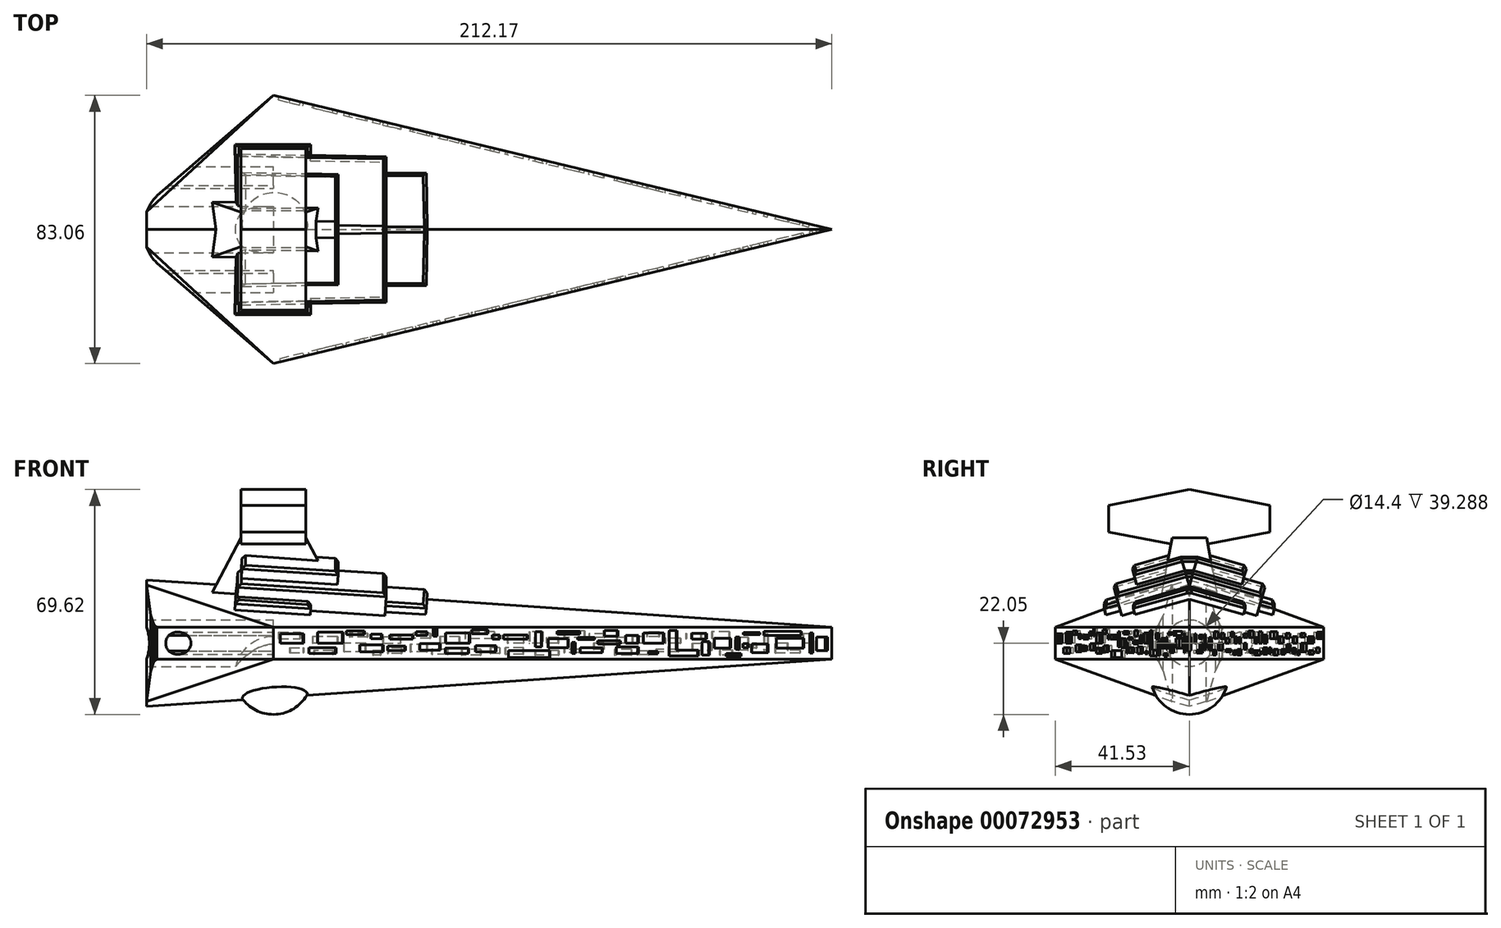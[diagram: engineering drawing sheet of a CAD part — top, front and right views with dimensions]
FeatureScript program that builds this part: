
annotation { "Feature Type Name" : "Feature", "Feature Type Description" : "" }
export const myFeature = defineFeature(function(context is Context, id is Id, definition is map)
    precondition{}
    {
        {
            var Q0;
            Q0=qCreatedBy(makeId("Top.planeOp"),FACE);
            var sketch = newSketch(context, id + "F0", { "sketchPlane" : qUnion([Q0])});
            skLineSegment(sketch, "E0", {"start": v(0, -41.53) * mm, "end": v(-48.04, 0) * mm});
            skLineSegment(sketch, "E1", {"start": v(-48.04, 0) * mm, "end": v(0, 41.53) * mm});
            skLineSegment(sketch, "E2", {"start": v(0, 41.53) * mm, "end": v(172.88, 0) * mm});
            skLineSegment(sketch, "E3", {"start": v(172.88, 0) * mm, "end": v(0, -41.53) * mm});
            skSolve(sketch);
        }
        {
            var Q0;
            Q0=makeQuery(id+"F0.imprint","IMPRINT",FACE,{"disambiguationData":[TD([[makeQuery(id+"F0.imprint","IMPRINT",EDGE,{"derivedFrom":sQuery(id+"F0.wireOp",EDGE,"E0")}),-1.0]])]});
            extrude(context, id + "F1", {"entities" : qUnion([Q0]), "depth" : 5 * mm});
        }
        {
            var Q0;
            Q0=qCreatedBy(makeId("Top.planeOp"),FACE);
            cPlane(context, id + "F2", {"entities" : qUnion([Q0]), "cplaneType" : CPlaneType.OFFSET, "offset" : 20 * mm, "width" : 150 * mm, "height" : 150 * mm});
        }
        {
            var Q0;
            Q0=qCreatedBy(id+"F2.planeOp",FACE);
            var sketch = newSketch(context, id + "F3", { "sketchPlane" : qUnion([Q0])});
            skPoint(sketch, "E4", {"position": v(-45.15, 0) * mm});
            skSolve(sketch);
        }
        {
            var Q1;
            Q1=sQuery(id+"F3.wireOp",VERTEX,"E4");
            var Q2;
            Q2=makeQuery(id+"F1.opExtrude","CAP_FACE",FACE,{"disambiguationData":[OSD([sQuery(id+"F0.wireOp",EDGE,"E0"),sQuery(id+"F0.wireOp",EDGE,"E1"),sQuery(id+"F0.wireOp",EDGE,"E2"),sQuery(id+"F0.wireOp",EDGE,"E3")])],"isStart":false});
            loft(context, id + "F4", {"operationType" : NewBodyOperationType.ADD, "sheetProfilesArray" : [{ "sheetProfileEntities" : qUnion([Q1]) }, { "sheetProfileEntities" : qUnion([Q2]) }]});
        }
        {
            var Q0;
            Q0=makeQuery(id+"F1.opExtrude","SWEPT_BODY",BODY,{"disambiguationData":[OSD([sQuery(id+"F0.wireOp",EDGE,"E0"),sQuery(id+"F0.wireOp",EDGE,"E1"),sQuery(id+"F0.wireOp",EDGE,"E2"),sQuery(id+"F0.wireOp",EDGE,"E3")])]});
            var Q1;
            Q1=qCreatedBy(makeId("Top.planeOp"),FACE);
            mirror(context, id + "F5", {"operationType" : NewBodyOperationType.ADD, "entities" : qUnion([Q0]), "mirrorPlane" : qUnion([Q1])});
        }
        {
            var Q0;
            {var subQ0=makeQuery(id+"F1.opExtrude","SWEPT_EDGE",EDGE,{"disambiguationData":[OSD([sQuery(id+"F0.wireOp",EDGE,"E0"),sQuery(id+"F0.wireOp",EDGE,"E1")])]});Q0=makeQuery(id+"F5.boolean.opBoolean","MERGE",EDGE,{"derivedFrom":[subQ0,makeQuery(id+"F5.opPattern","COPY",EDGE,{"derivedFrom":subQ0,"instanceName":"1"})]});}
            chamfer(context, id + "F6", {"entities" : qUnion([Q0]), "width" : 10 * mm, "tangentPropagation" : true});
        }
        {
            var Q0;
            {var subQ0=sQuery(id+"F0.wireOp",EDGE,"E0");var subQ1=makeQuery(id+"F1.opExtrude","SWEPT_FACE",FACE,{"disambiguationData":[OSD([subQ0])]});var subQ2=makeQuery(id+"F1.opExtrude","SWEPT_EDGE",EDGE,{"disambiguationData":[OSD([subQ0,sQuery(id+"F0.wireOp",EDGE,"E1")])]});Q0=makeQuery(id+"F6.opChamfer","BLEND_EDGE",EDGE,{"blendedFrom":[makeQuery(id+"F5.boolean.opBoolean","MERGE",EDGE,{"derivedFrom":[subQ2,makeQuery(id+"F5.opPattern","COPY",EDGE,{"derivedFrom":subQ2,"instanceName":"1"})]}),makeQuery(id+"F5.boolean.opBoolean","MERGE",FACE,{"derivedFrom":[subQ1,makeQuery(id+"F5.opPattern","COPY",FACE,{"derivedFrom":subQ1,"instanceName":"1"})]})],"blendedInto":[makeQuery(id+"F5.boolean.opBoolean","MERGE",FACE,{"derivedFrom":[subQ1,makeQuery(id+"F5.opPattern","COPY",FACE,{"derivedFrom":subQ1,"instanceName":"1"})]})]});}
            chamfer(context, id + "F7", {"entities" : qUnion([Q0]), "width" : 5 * mm, "tangentPropagation" : true});
        }
        {
            var Q0;
            {var subQ0=sQuery(id+"F0.wireOp",EDGE,"E1");var subQ1=makeQuery(id+"F1.opExtrude","SWEPT_FACE",FACE,{"disambiguationData":[OSD([subQ0])]});var subQ2=makeQuery(id+"F1.opExtrude","SWEPT_EDGE",EDGE,{"disambiguationData":[OSD([sQuery(id+"F0.wireOp",EDGE,"E0"),subQ0])]});Q0=makeQuery(id+"F6.opChamfer","BLEND_EDGE",EDGE,{"blendedFrom":[makeQuery(id+"F5.boolean.opBoolean","MERGE",EDGE,{"derivedFrom":[subQ2,makeQuery(id+"F5.opPattern","COPY",EDGE,{"derivedFrom":subQ2,"instanceName":"1"})]}),makeQuery(id+"F5.boolean.opBoolean","MERGE",FACE,{"derivedFrom":[subQ1,makeQuery(id+"F5.opPattern","COPY",FACE,{"derivedFrom":subQ1,"instanceName":"1"})]})],"blendedInto":[makeQuery(id+"F5.boolean.opBoolean","MERGE",FACE,{"derivedFrom":[subQ1,makeQuery(id+"F5.opPattern","COPY",FACE,{"derivedFrom":subQ1,"instanceName":"1"})]})]});}
            chamfer(context, id + "F8", {"entities" : qUnion([Q0]), "width" : 5 * mm, "tangentPropagation" : true});
        }
        {
            var Q0;
            {var subQ0=sQuery(id+"F0.wireOp",EDGE,"E1");var subQ1=makeQuery(id+"F1.opExtrude","SWEPT_FACE",FACE,{"disambiguationData":[OSD([subQ0])]});var subQ2=makeQuery(id+"F5.boolean.opBoolean","MERGE",FACE,{"derivedFrom":[subQ1,makeQuery(id+"F5.opPattern","COPY",FACE,{"derivedFrom":subQ1,"instanceName":"1"})]});var subQ3=makeQuery(id+"F1.opExtrude","SWEPT_EDGE",EDGE,{"disambiguationData":[OSD([sQuery(id+"F0.wireOp",EDGE,"E0"),subQ0])]});Q0=makeQuery(id+"F8.opChamfer","BLEND_EDGE",EDGE,{"blendedFrom":[makeQuery(id+"F6.opChamfer","BLEND_EDGE",EDGE,{"blendedFrom":[makeQuery(id+"F5.boolean.opBoolean","MERGE",EDGE,{"derivedFrom":[subQ3,makeQuery(id+"F5.opPattern","COPY",EDGE,{"derivedFrom":subQ3,"instanceName":"1"})]}),subQ2],"blendedInto":[subQ2]}),subQ2],"blendedInto":[subQ2]});}
            var Q1;
            {var subQ0=sQuery(id+"F0.wireOp",EDGE,"E0");var subQ1=makeQuery(id+"F1.opExtrude","SWEPT_FACE",FACE,{"disambiguationData":[OSD([subQ0])]});var subQ2=makeQuery(id+"F5.boolean.opBoolean","MERGE",FACE,{"derivedFrom":[subQ1,makeQuery(id+"F5.opPattern","COPY",FACE,{"derivedFrom":subQ1,"instanceName":"1"})]});var subQ3=makeQuery(id+"F1.opExtrude","SWEPT_EDGE",EDGE,{"disambiguationData":[OSD([subQ0,sQuery(id+"F0.wireOp",EDGE,"E1")])]});Q1=makeQuery(id+"F7.opChamfer","BLEND_EDGE",EDGE,{"blendedFrom":[makeQuery(id+"F6.opChamfer","BLEND_EDGE",EDGE,{"blendedFrom":[makeQuery(id+"F5.boolean.opBoolean","MERGE",EDGE,{"derivedFrom":[subQ3,makeQuery(id+"F5.opPattern","COPY",EDGE,{"derivedFrom":subQ3,"instanceName":"1"})]}),subQ2],"blendedInto":[subQ2]}),subQ2],"blendedInto":[subQ2]});}
            chamfer(context, id + "F9", {"entities" : qUnion([Q0, Q1]), "width" : 5 * mm, "tangentPropagation" : true});
        }
        {
            var Q0;
            {var subQ0=sQuery(id+"F0.wireOp",EDGE,"E1");var subQ1=makeQuery(id+"F1.opExtrude","SWEPT_FACE",FACE,{"disambiguationData":[OSD([subQ0])]});var subQ2=makeQuery(id+"F5.boolean.opBoolean","MERGE",FACE,{"derivedFrom":[subQ1,makeQuery(id+"F5.opPattern","COPY",FACE,{"derivedFrom":subQ1,"instanceName":"1"})]});var subQ3=subQ2;var subQ4=makeQuery(id+"F1.opExtrude","SWEPT_EDGE",EDGE,{"disambiguationData":[OSD([sQuery(id+"F0.wireOp",EDGE,"E0"),subQ0])]});Q0=makeQuery(id+"F9.opChamfer","BLEND_EDGE",EDGE,{"blendedFrom":[makeQuery(id+"F8.opChamfer","BLEND_EDGE",EDGE,{"blendedFrom":[makeQuery(id+"F6.opChamfer","BLEND_EDGE",EDGE,{"blendedFrom":[makeQuery(id+"F5.boolean.opBoolean","MERGE",EDGE,{"derivedFrom":[subQ4,makeQuery(id+"F5.opPattern","COPY",EDGE,{"derivedFrom":subQ4,"instanceName":"1"})]}),subQ2],"blendedInto":[subQ2]}),subQ3],"blendedInto":[subQ3]}),subQ3],"blendedInto":[subQ3]});}
            var Q1;
            {var subQ0=sQuery(id+"F0.wireOp",EDGE,"E0");var subQ1=makeQuery(id+"F1.opExtrude","SWEPT_FACE",FACE,{"disambiguationData":[OSD([subQ0])]});var subQ2=makeQuery(id+"F5.boolean.opBoolean","MERGE",FACE,{"derivedFrom":[subQ1,makeQuery(id+"F5.opPattern","COPY",FACE,{"derivedFrom":subQ1,"instanceName":"1"})]});var subQ3=subQ2;var subQ4=makeQuery(id+"F1.opExtrude","SWEPT_EDGE",EDGE,{"disambiguationData":[OSD([subQ0,sQuery(id+"F0.wireOp",EDGE,"E1")])]});Q1=makeQuery(id+"F9.opChamfer","BLEND_EDGE",EDGE,{"blendedFrom":[makeQuery(id+"F7.opChamfer","BLEND_EDGE",EDGE,{"blendedFrom":[makeQuery(id+"F6.opChamfer","BLEND_EDGE",EDGE,{"blendedFrom":[makeQuery(id+"F5.boolean.opBoolean","MERGE",EDGE,{"derivedFrom":[subQ4,makeQuery(id+"F5.opPattern","COPY",EDGE,{"derivedFrom":subQ4,"instanceName":"1"})]}),subQ2],"blendedInto":[subQ2]}),subQ3],"blendedInto":[subQ3]}),subQ3],"blendedInto":[subQ3]});}
            chamfer(context, id + "F10", {"entities" : qUnion([Q0, Q1]), "width" : 5 * mm, "tangentPropagation" : true});
        }
        {
            var Q0;
            {var subQ0=sQuery(id+"F0.wireOp",EDGE,"E1");var subQ1=makeQuery(id+"F1.opExtrude","SWEPT_FACE",FACE,{"disambiguationData":[OSD([subQ0])]});var subQ2=makeQuery(id+"F5.boolean.opBoolean","MERGE",FACE,{"derivedFrom":[subQ1,makeQuery(id+"F5.opPattern","COPY",FACE,{"derivedFrom":subQ1,"instanceName":"1"})]});var subQ3=subQ2;var subQ4=subQ3;var subQ5=makeQuery(id+"F1.opExtrude","SWEPT_EDGE",EDGE,{"disambiguationData":[OSD([sQuery(id+"F0.wireOp",EDGE,"E0"),subQ0])]});Q0=makeQuery(id+"F10.opChamfer","BLEND_EDGE",EDGE,{"blendedFrom":[makeQuery(id+"F9.opChamfer","BLEND_EDGE",EDGE,{"blendedFrom":[makeQuery(id+"F8.opChamfer","BLEND_EDGE",EDGE,{"blendedFrom":[makeQuery(id+"F6.opChamfer","BLEND_EDGE",EDGE,{"blendedFrom":[makeQuery(id+"F5.boolean.opBoolean","MERGE",EDGE,{"derivedFrom":[subQ5,makeQuery(id+"F5.opPattern","COPY",EDGE,{"derivedFrom":subQ5,"instanceName":"1"})]}),subQ2],"blendedInto":[subQ2]}),subQ3],"blendedInto":[subQ3]}),subQ4],"blendedInto":[subQ4]}),subQ4],"blendedInto":[subQ4]});}
            var Q1;
            {var subQ0=sQuery(id+"F0.wireOp",EDGE,"E0");var subQ1=makeQuery(id+"F1.opExtrude","SWEPT_FACE",FACE,{"disambiguationData":[OSD([subQ0])]});var subQ2=makeQuery(id+"F5.boolean.opBoolean","MERGE",FACE,{"derivedFrom":[subQ1,makeQuery(id+"F5.opPattern","COPY",FACE,{"derivedFrom":subQ1,"instanceName":"1"})]});var subQ3=subQ2;var subQ4=subQ3;var subQ5=makeQuery(id+"F1.opExtrude","SWEPT_EDGE",EDGE,{"disambiguationData":[OSD([subQ0,sQuery(id+"F0.wireOp",EDGE,"E1")])]});Q1=makeQuery(id+"F10.opChamfer","BLEND_EDGE",EDGE,{"blendedFrom":[makeQuery(id+"F9.opChamfer","BLEND_EDGE",EDGE,{"blendedFrom":[makeQuery(id+"F7.opChamfer","BLEND_EDGE",EDGE,{"blendedFrom":[makeQuery(id+"F6.opChamfer","BLEND_EDGE",EDGE,{"blendedFrom":[makeQuery(id+"F5.boolean.opBoolean","MERGE",EDGE,{"derivedFrom":[subQ5,makeQuery(id+"F5.opPattern","COPY",EDGE,{"derivedFrom":subQ5,"instanceName":"1"})]}),subQ2],"blendedInto":[subQ2]}),subQ3],"blendedInto":[subQ3]}),subQ4],"blendedInto":[subQ4]}),subQ4],"blendedInto":[subQ4]});}
            chamfer(context, id + "F11", {"entities" : qUnion([Q0, Q1]), "width" : 5 * mm, "tangentPropagation" : true});
        }
        {
            var Q0;
            {var subQ0=sQuery(id+"F0.wireOp",EDGE,"E1");var subQ1=makeQuery(id+"F1.opExtrude","SWEPT_FACE",FACE,{"disambiguationData":[OSD([subQ0])]});var subQ2=makeQuery(id+"F5.boolean.opBoolean","MERGE",FACE,{"derivedFrom":[subQ1,makeQuery(id+"F5.opPattern","COPY",FACE,{"derivedFrom":subQ1,"instanceName":"1"})]});var subQ3=subQ2;var subQ4=subQ3;var subQ5=subQ4;var subQ6=makeQuery(id+"F1.opExtrude","SWEPT_EDGE",EDGE,{"disambiguationData":[OSD([sQuery(id+"F0.wireOp",EDGE,"E0"),subQ0])]});Q0=makeQuery(id+"F11.opChamfer","BLEND_EDGE",EDGE,{"blendedFrom":[makeQuery(id+"F10.opChamfer","BLEND_EDGE",EDGE,{"blendedFrom":[makeQuery(id+"F9.opChamfer","BLEND_EDGE",EDGE,{"blendedFrom":[makeQuery(id+"F8.opChamfer","BLEND_EDGE",EDGE,{"blendedFrom":[makeQuery(id+"F6.opChamfer","BLEND_EDGE",EDGE,{"blendedFrom":[makeQuery(id+"F5.boolean.opBoolean","MERGE",EDGE,{"derivedFrom":[subQ6,makeQuery(id+"F5.opPattern","COPY",EDGE,{"derivedFrom":subQ6,"instanceName":"1"})]}),subQ2],"blendedInto":[subQ2]}),subQ3],"blendedInto":[subQ3]}),subQ4],"blendedInto":[subQ4]}),subQ5],"blendedInto":[subQ5]}),subQ5],"blendedInto":[subQ5]});}
            var Q1;
            {var subQ0=sQuery(id+"F0.wireOp",EDGE,"E0");var subQ1=makeQuery(id+"F1.opExtrude","SWEPT_FACE",FACE,{"disambiguationData":[OSD([subQ0])]});var subQ2=makeQuery(id+"F5.boolean.opBoolean","MERGE",FACE,{"derivedFrom":[subQ1,makeQuery(id+"F5.opPattern","COPY",FACE,{"derivedFrom":subQ1,"instanceName":"1"})]});var subQ3=subQ2;var subQ4=subQ3;var subQ5=subQ4;var subQ6=makeQuery(id+"F1.opExtrude","SWEPT_EDGE",EDGE,{"disambiguationData":[OSD([subQ0,sQuery(id+"F0.wireOp",EDGE,"E1")])]});Q1=makeQuery(id+"F11.opChamfer","BLEND_EDGE",EDGE,{"blendedFrom":[makeQuery(id+"F10.opChamfer","BLEND_EDGE",EDGE,{"blendedFrom":[makeQuery(id+"F9.opChamfer","BLEND_EDGE",EDGE,{"blendedFrom":[makeQuery(id+"F7.opChamfer","BLEND_EDGE",EDGE,{"blendedFrom":[makeQuery(id+"F6.opChamfer","BLEND_EDGE",EDGE,{"blendedFrom":[makeQuery(id+"F5.boolean.opBoolean","MERGE",EDGE,{"derivedFrom":[subQ6,makeQuery(id+"F5.opPattern","COPY",EDGE,{"derivedFrom":subQ6,"instanceName":"1"})]}),subQ2],"blendedInto":[subQ2]}),subQ3],"blendedInto":[subQ3]}),subQ4],"blendedInto":[subQ4]}),subQ5],"blendedInto":[subQ5]}),subQ5],"blendedInto":[subQ5]});}
            chamfer(context, id + "F12", {"entities" : qUnion([Q0, Q1]), "width" : 5 * mm, "tangentPropagation" : true});
        }
        {
            var Q0;
            Q0=qCreatedBy(makeId("Right.planeOp"),FACE);
            var sketch = newSketch(context, id + "F13", { "sketchPlane" : qUnion([Q0])});
            skCircle(sketch, "E5", {"center": v(0, 0) * mm, "radius": 7.2 * mm});
            skCircle(sketch, "E6", {"center": v(16.02, 0) * mm, "radius": 3.47 * mm});
            skCircle(sketch, "E7", {"center": v(-16.62, 0) * mm, "radius": 3.92 * mm});
            skSolve(sketch);
        }
        {
            var Q0;
            Q0 = qSketchRegion(id + "F13", true);
            extrude(context, id + "F14", {"entities" : qUnion([Q0]), "operationType" : NewBodyOperationType.REMOVE, "oppositeDirection" : true, "depth" : 99.65 * mm});
        }
        {
            var Q0;
            {var subQ0=makeQuery(id+"F1.opExtrude","SWEPT_FACE",FACE,{"disambiguationData":[OSD([sQuery(id+"F0.wireOp",EDGE,"E3")])]});Q0=makeQuery(id+"F5.boolean.opBoolean","MERGE",FACE,{"derivedFrom":[subQ0,makeQuery(id+"F5.opPattern","COPY",FACE,{"derivedFrom":subQ0,"instanceName":"1"})]});}
            var sketch = newSketch(context, id + "F15", { "sketchPlane" : qUnion([Q0])});
            skLineSegment(sketch, "E8.rect.bottom", {"start": v(0, 0) * mm, "end": v(-7.53, 0) * mm});
            skLineSegment(sketch, "E8.rect.top", {"start": v(0, 2.86) * mm, "end": v(-7.53, 2.86) * mm});
            skLineSegment(sketch, "E8.rect.left", {"start": v(0, 0) * mm, "end": v(0, 2.86) * mm});
            skLineSegment(sketch, "E8.rect.right", {"start": v(-7.53, 0) * mm, "end": v(-7.53, 2.86) * mm});
            skPoint(sketch, "E8.rect.middle", {"position": v(-3.77, 1.43) * mm});
            skLineSegment(sketch, "E9.rect.bottom", {"start": v(10.31, -3.23) * mm, "end": v(1.65, -3.23) * mm});
            skLineSegment(sketch, "E9.rect.top", {"start": v(10.31, -1.43) * mm, "end": v(1.65, -1.43) * mm});
            skLineSegment(sketch, "E9.rect.left", {"start": v(10.31, -3.23) * mm, "end": v(10.31, -1.43) * mm});
            skLineSegment(sketch, "E9.rect.right", {"start": v(1.65, -3.23) * mm, "end": v(1.65, -1.43) * mm});
            skPoint(sketch, "E9.rect.middle", {"position": v(5.98, -2.33) * mm});
            skLineSegment(sketch, "E10.rect.bottom", {"start": v(12.48, 0) * mm, "end": v(4.43, 0) * mm});
            skLineSegment(sketch, "E10.rect.top", {"start": v(12.48, 3.46) * mm, "end": v(4.43, 3.46) * mm});
            skLineSegment(sketch, "E10.rect.left", {"start": v(12.48, 0) * mm, "end": v(12.48, 3.46) * mm});
            skLineSegment(sketch, "E10.rect.right", {"start": v(4.43, 0) * mm, "end": v(4.43, 3.46) * mm});
            skPoint(sketch, "E10.rect.middle", {"position": v(8.46, 1.73) * mm});
            skLineSegment(sketch, "E11.rect.bottom", {"start": v(25.32, -2.63) * mm, "end": v(17.9, -2.63) * mm});
            skLineSegment(sketch, "E11.rect.top", {"start": v(25.32, -0.53) * mm, "end": v(17.9, -0.53) * mm});
            skLineSegment(sketch, "E11.rect.left", {"start": v(25.32, -2.63) * mm, "end": v(25.32, -0.53) * mm});
            skLineSegment(sketch, "E11.rect.right", {"start": v(17.9, -2.63) * mm, "end": v(17.9, -0.53) * mm});
            skPoint(sketch, "E11.rect.middle", {"position": v(21.6, -1.58) * mm});
            skLineSegment(sketch, "E12.rect.bottom", {"start": v(34.76, 1.28) * mm, "end": v(27.33, 1.28) * mm});
            skLineSegment(sketch, "E12.rect.top", {"start": v(34.76, 2.48) * mm, "end": v(27.33, 2.48) * mm});
            skLineSegment(sketch, "E12.rect.left", {"start": v(34.76, 1.28) * mm, "end": v(34.76, 2.48) * mm});
            skLineSegment(sketch, "E12.rect.right", {"start": v(27.33, 1.28) * mm, "end": v(27.33, 2.48) * mm});
            skPoint(sketch, "E12.rect.middle", {"position": v(31.04, 1.88) * mm});
            skLineSegment(sketch, "E13.rect.bottom", {"start": v(43.42, -2.18) * mm, "end": v(36.92, -2.18) * mm});
            skLineSegment(sketch, "E13.rect.top", {"start": v(43.42, -0.08) * mm, "end": v(36.92, -0.08) * mm});
            skLineSegment(sketch, "E13.rect.left", {"start": v(43.42, -2.18) * mm, "end": v(43.42, -0.08) * mm});
            skLineSegment(sketch, "E13.rect.right", {"start": v(36.92, -2.18) * mm, "end": v(36.92, -0.08) * mm});
            skPoint(sketch, "E13.rect.middle", {"position": v(40.17, -1.13) * mm});
            skLineSegment(sketch, "E14.rect.bottom", {"start": v(52.86, 0) * mm, "end": v(45.12, 0) * mm});
            skLineSegment(sketch, "E14.rect.top", {"start": v(52.86, 3.16) * mm, "end": v(45.12, 3.16) * mm});
            skLineSegment(sketch, "E14.rect.left", {"start": v(52.86, 0) * mm, "end": v(52.86, 3.16) * mm});
            skLineSegment(sketch, "E14.rect.right", {"start": v(45.12, 0) * mm, "end": v(45.12, 3.16) * mm});
            skPoint(sketch, "E14.rect.middle", {"position": v(48.99, 1.58) * mm});
            skLineSegment(sketch, "E15.rect.bottom", {"start": v(61.21, -2.63) * mm, "end": v(54.71, -2.63) * mm});
            skLineSegment(sketch, "E15.rect.top", {"start": v(61.21, -0.83) * mm, "end": v(54.71, -0.83) * mm});
            skLineSegment(sketch, "E15.rect.left", {"start": v(61.21, -2.63) * mm, "end": v(61.21, -0.83) * mm});
            skLineSegment(sketch, "E15.rect.right", {"start": v(54.71, -2.63) * mm, "end": v(54.71, -0.83) * mm});
            skPoint(sketch, "E15.rect.middle", {"position": v(57.96, -1.73) * mm});
            skLineSegment(sketch, "E16.rect.bottom", {"start": v(71.27, 1.28) * mm, "end": v(63.53, 1.28) * mm});
            skLineSegment(sketch, "E16.rect.top", {"start": v(71.27, 2.48) * mm, "end": v(63.53, 2.48) * mm});
            skLineSegment(sketch, "E16.rect.left", {"start": v(71.27, 1.28) * mm, "end": v(71.27, 2.48) * mm});
            skLineSegment(sketch, "E16.rect.right", {"start": v(63.53, 1.28) * mm, "end": v(63.53, 2.48) * mm});
            skPoint(sketch, "E16.rect.middle", {"position": v(67.4, 1.88) * mm});
            skLineSegment(sketch, "E17.rect.bottom", {"start": v(78.38, -2.33) * mm, "end": v(65.08, -2.33) * mm});
            skLineSegment(sketch, "E17.rect.top", {"start": v(78.38, -4.44) * mm, "end": v(65.08, -4.44) * mm});
            skLineSegment(sketch, "E17.rect.left", {"start": v(78.38, -2.33) * mm, "end": v(78.38, -4.44) * mm});
            skLineSegment(sketch, "E17.rect.right", {"start": v(65.08, -2.33) * mm, "end": v(65.08, -4.44) * mm});
            skPoint(sketch, "E17.rect.middle", {"position": v(71.73, -3.38) * mm});
            skLineSegment(sketch, "E18.rect.bottom", {"start": v(84.26, -1.43) * mm, "end": v(77.76, -1.43) * mm});
            skLineSegment(sketch, "E18.rect.top", {"start": v(84.26, 1.43) * mm, "end": v(77.76, 1.43) * mm});
            skLineSegment(sketch, "E18.rect.left", {"start": v(84.26, -1.43) * mm, "end": v(84.26, 1.43) * mm});
            skLineSegment(sketch, "E18.rect.right", {"start": v(77.76, -1.43) * mm, "end": v(77.76, 1.43) * mm});
            skPoint(sketch, "E18.rect.middle", {"position": v(81.01, 0) * mm});
            skLineSegment(sketch, "E19.rect.bottom", {"start": v(95.1, -1.43) * mm, "end": v(87.98, -1.43) * mm});
            skLineSegment(sketch, "E19.rect.top", {"start": v(95.1, -2.93) * mm, "end": v(87.98, -2.93) * mm});
            skLineSegment(sketch, "E19.rect.left", {"start": v(95.1, -1.43) * mm, "end": v(95.1, -2.93) * mm});
            skLineSegment(sketch, "E19.rect.right", {"start": v(87.98, -1.43) * mm, "end": v(87.98, -2.93) * mm});
            skPoint(sketch, "E19.rect.middle", {"position": v(91.53, -2.18) * mm});
            skLineSegment(sketch, "E20.rect.bottom", {"start": v(100.04, 2.18) * mm, "end": v(95.71, 2.18) * mm});
            skLineSegment(sketch, "E20.rect.top", {"start": v(100.04, 3.99) * mm, "end": v(95.71, 3.99) * mm});
            skLineSegment(sketch, "E20.rect.left", {"start": v(100.04, 2.18) * mm, "end": v(100.04, 3.99) * mm});
            skLineSegment(sketch, "E20.rect.right", {"start": v(95.71, 2.18) * mm, "end": v(95.71, 3.99) * mm});
            skPoint(sketch, "E20.rect.middle", {"position": v(97.88, 3.08) * mm});
            skLineSegment(sketch, "E21.rect.bottom", {"start": v(106.54, -1.13) * mm, "end": v(99.42, -1.13) * mm});
            skLineSegment(sketch, "E21.rect.top", {"start": v(106.54, -3.23) * mm, "end": v(99.42, -3.23) * mm});
            skLineSegment(sketch, "E21.rect.left", {"start": v(106.54, -1.13) * mm, "end": v(106.54, -3.23) * mm});
            skLineSegment(sketch, "E21.rect.right", {"start": v(99.42, -1.13) * mm, "end": v(99.42, -3.23) * mm});
            skPoint(sketch, "E21.rect.middle", {"position": v(102.98, -2.18) * mm});
            skLineSegment(sketch, "E22.rect.bottom", {"start": v(114.59, 0) * mm, "end": v(108.09, 0) * mm});
            skLineSegment(sketch, "E22.rect.top", {"start": v(114.59, 3.16) * mm, "end": v(108.09, 3.16) * mm});
            skLineSegment(sketch, "E22.rect.left", {"start": v(114.59, 0) * mm, "end": v(114.59, 3.16) * mm});
            skLineSegment(sketch, "E22.rect.right", {"start": v(108.09, 0) * mm, "end": v(108.09, 3.16) * mm});
            skPoint(sketch, "E22.rect.middle", {"position": v(111.34, 1.58) * mm});
            skLineSegment(sketch, "E23.rect.bottom", {"start": v(125.57, -2.18) * mm, "end": v(118.76, -2.18) * mm});
            skLineSegment(sketch, "E23.rect.top", {"start": v(125.57, -3.99) * mm, "end": v(118.76, -3.99) * mm});
            skLineSegment(sketch, "E23.rect.left", {"start": v(125.57, -2.18) * mm, "end": v(125.57, -3.99) * mm});
            skLineSegment(sketch, "E23.rect.right", {"start": v(118.76, -2.18) * mm, "end": v(118.76, -3.99) * mm});
            skPoint(sketch, "E23.rect.middle", {"position": v(122.17, -3.08) * mm});
            skLineSegment(sketch, "E24.rect.bottom", {"start": v(128.2, 1.28) * mm, "end": v(123.56, 1.28) * mm});
            skLineSegment(sketch, "E24.rect.top", {"start": v(128.2, 3.08) * mm, "end": v(123.56, 3.08) * mm});
            skLineSegment(sketch, "E24.rect.left", {"start": v(128.2, 1.28) * mm, "end": v(128.2, 3.08) * mm});
            skLineSegment(sketch, "E24.rect.right", {"start": v(123.56, 1.28) * mm, "end": v(123.56, 3.08) * mm});
            skPoint(sketch, "E24.rect.middle", {"position": v(125.88, 2.18) * mm});
            skLineSegment(sketch, "E25.rect.bottom", {"start": v(135.94, -1.58) * mm, "end": v(130.67, -1.58) * mm});
            skLineSegment(sketch, "E25.rect.top", {"start": v(135.94, 1.58) * mm, "end": v(130.67, 1.58) * mm});
            skLineSegment(sketch, "E25.rect.left", {"start": v(135.94, -1.58) * mm, "end": v(135.94, 1.58) * mm});
            skLineSegment(sketch, "E25.rect.right", {"start": v(130.67, -1.58) * mm, "end": v(130.67, 1.58) * mm});
            skPoint(sketch, "E25.rect.middle", {"position": v(133.3, 0) * mm});
            skLineSegment(sketch, "E26.rect.bottom", {"start": v(147.85, -2.93) * mm, "end": v(142.59, -2.93) * mm});
            skLineSegment(sketch, "E26.rect.top", {"start": v(147.85, -0.23) * mm, "end": v(142.59, -0.23) * mm});
            skLineSegment(sketch, "E26.rect.left", {"start": v(147.85, -2.93) * mm, "end": v(147.85, -0.23) * mm});
            skLineSegment(sketch, "E26.rect.right", {"start": v(142.59, -2.93) * mm, "end": v(142.59, -0.23) * mm});
            skPoint(sketch, "E26.rect.middle", {"position": v(145.22, -1.58) * mm});
            skLineSegment(sketch, "E27.rect.bottom", {"start": v(145.22, 2.63) * mm, "end": v(139.96, 2.63) * mm});
            skLineSegment(sketch, "E27.rect.top", {"start": v(145.22, 3.23) * mm, "end": v(139.96, 3.23) * mm});
            skLineSegment(sketch, "E27.rect.left", {"start": v(145.22, 2.63) * mm, "end": v(145.22, 3.23) * mm});
            skLineSegment(sketch, "E27.rect.right", {"start": v(139.96, 2.63) * mm, "end": v(139.96, 3.23) * mm});
            skPoint(sketch, "E27.rect.middle", {"position": v(142.59, 2.93) * mm});
            skLineSegment(sketch, "E28.rect.bottom", {"start": v(159.14, -1.58) * mm, "end": v(150.48, -1.58) * mm});
            skLineSegment(sketch, "E28.rect.top", {"start": v(159.14, 1.58) * mm, "end": v(150.48, 1.58) * mm});
            skLineSegment(sketch, "E28.rect.left", {"start": v(159.14, -1.58) * mm, "end": v(159.14, 1.58) * mm});
            skLineSegment(sketch, "E28.rect.right", {"start": v(150.48, -1.58) * mm, "end": v(150.48, 1.58) * mm});
            skPoint(sketch, "E28.rect.middle", {"position": v(154.8, 0) * mm});
            skLineSegment(sketch, "E29.bottom", {"start": v(19.25, 2.71) * mm, "end": v(13.6, 2.71) * mm});
            skLineSegment(sketch, "E29.top", {"start": v(19.25, 3.8) * mm, "end": v(13.6, 3.8) * mm});
            skLineSegment(sketch, "E29.left", {"start": v(19.25, 2.71) * mm, "end": v(19.25, 3.8) * mm});
            skLineSegment(sketch, "E29.right", {"start": v(13.6, 2.71) * mm, "end": v(13.6, 3.8) * mm});
            skPoint(sketch, "E29.middle", {"position": v(16.43, 3.26) * mm});
            skLineSegment(sketch, "E30.bottom", {"start": v(24.94, 1.38) * mm, "end": v(21.4, 1.38) * mm});
            skLineSegment(sketch, "E30.top", {"start": v(24.94, 2.73) * mm, "end": v(21.4, 2.73) * mm});
            skLineSegment(sketch, "E30.left", {"start": v(24.94, 1.38) * mm, "end": v(24.94, 2.73) * mm});
            skLineSegment(sketch, "E30.right", {"start": v(21.4, 1.38) * mm, "end": v(21.4, 2.73) * mm});
            skPoint(sketch, "E30.middle", {"position": v(23.17, 2.05) * mm});
            skLineSegment(sketch, "E31.bottom", {"start": v(32.3, -2.24) * mm, "end": v(26.73, -2.24) * mm});
            skLineSegment(sketch, "E31.top", {"start": v(32.3, -0.94) * mm, "end": v(26.73, -0.94) * mm});
            skLineSegment(sketch, "E31.left", {"start": v(32.3, -2.24) * mm, "end": v(32.3, -0.94) * mm});
            skLineSegment(sketch, "E31.right", {"start": v(26.73, -2.24) * mm, "end": v(26.73, -0.94) * mm});
            skPoint(sketch, "E31.middle", {"position": v(29.51, -1.6) * mm});
            skLineSegment(sketch, "E32.bottom", {"start": v(39.33, 2.41) * mm, "end": v(35.72, 2.41) * mm});
            skLineSegment(sketch, "E32.top", {"start": v(39.33, 3.56) * mm, "end": v(35.72, 3.56) * mm});
            skLineSegment(sketch, "E32.left", {"start": v(39.33, 2.41) * mm, "end": v(39.33, 3.56) * mm});
            skLineSegment(sketch, "E32.right", {"start": v(35.72, 2.41) * mm, "end": v(35.72, 3.56) * mm});
            skPoint(sketch, "E32.middle", {"position": v(37.53, 2.98) * mm});
            skLineSegment(sketch, "E33.bottom", {"start": v(42.39, 2.14) * mm, "end": v(41.2, 2.14) * mm});
            skLineSegment(sketch, "E33.top", {"start": v(42.39, 4.39) * mm, "end": v(41.2, 4.39) * mm});
            skLineSegment(sketch, "E33.left", {"start": v(42.39, 2.14) * mm, "end": v(42.39, 4.39) * mm});
            skLineSegment(sketch, "E33.right", {"start": v(41.2, 2.14) * mm, "end": v(41.2, 4.39) * mm});
            skPoint(sketch, "E33.middle", {"position": v(41.8, 3.26) * mm});
            skLineSegment(sketch, "E34.bottom", {"start": v(52.53, -3.17) * mm, "end": v(45.07, -3.17) * mm});
            skLineSegment(sketch, "E34.top", {"start": v(52.53, -1.5) * mm, "end": v(45.07, -1.5) * mm});
            skLineSegment(sketch, "E34.left", {"start": v(52.53, -3.17) * mm, "end": v(52.53, -1.5) * mm});
            skLineSegment(sketch, "E34.right", {"start": v(45.07, -3.17) * mm, "end": v(45.07, -1.5) * mm});
            skPoint(sketch, "E34.middle", {"position": v(48.8, -2.34) * mm});
            skLineSegment(sketch, "E35.bottom", {"start": v(75.77, -1.09) * mm, "end": v(73.7, -1.09) * mm});
            skLineSegment(sketch, "E35.top", {"start": v(75.77, 3.53) * mm, "end": v(73.7, 3.53) * mm});
            skLineSegment(sketch, "E35.left", {"start": v(75.77, -1.09) * mm, "end": v(75.77, 3.53) * mm});
            skLineSegment(sketch, "E35.right", {"start": v(73.7, -1.09) * mm, "end": v(73.7, 3.53) * mm});
            skPoint(sketch, "E35.middle", {"position": v(74.74, 1.22) * mm});
            skLineSegment(sketch, "E36.bottom", {"start": v(58.56, 2.85) * mm, "end": v(53.51, 2.85) * mm});
            skLineSegment(sketch, "E36.top", {"start": v(58.56, 4.22) * mm, "end": v(53.51, 4.22) * mm});
            skLineSegment(sketch, "E36.left", {"start": v(58.56, 2.85) * mm, "end": v(58.56, 4.22) * mm});
            skLineSegment(sketch, "E36.right", {"start": v(53.51, 2.85) * mm, "end": v(53.51, 4.22) * mm});
            skPoint(sketch, "E36.middle", {"position": v(56.03, 3.53) * mm});
            skLineSegment(sketch, "E37.bottom", {"start": v(92.52, 1.19) * mm, "end": v(87.16, 1.19) * mm});
            skLineSegment(sketch, "E37.top", {"start": v(92.52, 1.72) * mm, "end": v(87.16, 1.72) * mm});
            skLineSegment(sketch, "E37.left", {"start": v(92.52, 1.19) * mm, "end": v(92.52, 1.72) * mm});
            skLineSegment(sketch, "E37.right", {"start": v(87.16, 1.19) * mm, "end": v(87.16, 1.72) * mm});
            skPoint(sketch, "E37.middle", {"position": v(89.84, 1.45) * mm});
            skLineSegment(sketch, "E38.bottom", {"start": v(87.93, 2.76) * mm, "end": v(80.69, 2.76) * mm});
            skLineSegment(sketch, "E38.top", {"start": v(87.93, 3.65) * mm, "end": v(80.69, 3.65) * mm});
            skLineSegment(sketch, "E38.left", {"start": v(87.93, 2.76) * mm, "end": v(87.93, 3.65) * mm});
            skLineSegment(sketch, "E38.right", {"start": v(80.69, 2.76) * mm, "end": v(80.69, 3.65) * mm});
            skPoint(sketch, "E38.middle", {"position": v(84.3, 3.2) * mm});
            skLineSegment(sketch, "E39.bottom", {"start": v(86.36, -3.16) * mm, "end": v(85.34, -3.16) * mm});
            skLineSegment(sketch, "E39.top", {"start": v(86.36, 0.3) * mm, "end": v(85.34, 0.3) * mm});
            skLineSegment(sketch, "E39.left", {"start": v(86.36, -3.16) * mm, "end": v(86.36, 0.3) * mm});
            skLineSegment(sketch, "E39.right", {"start": v(85.34, -3.16) * mm, "end": v(85.34, 0.3) * mm});
            skPoint(sketch, "E39.middle", {"position": v(85.85, -1.43) * mm});
            skLineSegment(sketch, "E40.bottom", {"start": v(106.54, 0) * mm, "end": v(102.48, 0) * mm});
            skLineSegment(sketch, "E40.top", {"start": v(106.54, 2.45) * mm, "end": v(102.48, 2.45) * mm});
            skLineSegment(sketch, "E40.left", {"start": v(106.54, 0) * mm, "end": v(106.54, 2.45) * mm});
            skLineSegment(sketch, "E40.right", {"start": v(102.48, 0) * mm, "end": v(102.48, 2.45) * mm});
            skPoint(sketch, "E40.middle", {"position": v(104.51, 1.22) * mm});
            skPoint(sketch, "E40.middle.positionSnap0", {"position": v(75.77, 1.22) * mm});
            skPoint(sketch, "E40.centerSnap0", {"position": v(75.77, 1.22) * mm});
            skLineSegment(sketch, "E41.bottom", {"start": v(118.76, -3.99) * mm, "end": v(116.37, -3.99) * mm});
            skLineSegment(sketch, "E41.top", {"start": v(118.76, 3.99) * mm, "end": v(116.37, 3.99) * mm});
            skLineSegment(sketch, "E41.left", {"start": v(118.76, -3.99) * mm, "end": v(118.76, 3.99) * mm});
            skLineSegment(sketch, "E41.right", {"start": v(116.37, -3.99) * mm, "end": v(116.37, 3.99) * mm});
            skPoint(sketch, "E41.middle", {"position": v(117.57, 0) * mm});
            skLineSegment(sketch, "E42.bottom", {"start": v(62.36, 1.28) * mm, "end": v(60.03, 1.28) * mm});
            skLineSegment(sketch, "E42.top", {"start": v(62.36, 2.58) * mm, "end": v(60.03, 2.58) * mm});
            skLineSegment(sketch, "E42.left", {"start": v(62.36, 1.28) * mm, "end": v(62.36, 2.58) * mm});
            skLineSegment(sketch, "E42.right", {"start": v(60.03, 1.28) * mm, "end": v(60.03, 2.58) * mm});
            skPoint(sketch, "E42.middle", {"position": v(61.2, 1.93) * mm});
            skLineSegment(sketch, "E43.bottom", {"start": v(112.64, -3.33) * mm, "end": v(109.83, -3.33) * mm});
            skLineSegment(sketch, "E43.top", {"start": v(112.64, -2.58) * mm, "end": v(109.83, -2.58) * mm});
            skLineSegment(sketch, "E43.left", {"start": v(112.64, -3.33) * mm, "end": v(112.64, -2.58) * mm});
            skLineSegment(sketch, "E43.right", {"start": v(109.83, -3.33) * mm, "end": v(109.83, -2.58) * mm});
            skPoint(sketch, "E43.middle", {"position": v(111.23, -2.96) * mm});
            skLineSegment(sketch, "E44.bottom", {"start": v(129.1, -3.7) * mm, "end": v(126.72, -3.7) * mm});
            skLineSegment(sketch, "E44.top", {"start": v(129.1, 0.54) * mm, "end": v(126.72, 0.54) * mm});
            skLineSegment(sketch, "E44.left", {"start": v(129.1, -3.7) * mm, "end": v(129.1, 0.54) * mm});
            skLineSegment(sketch, "E44.right", {"start": v(126.72, -3.7) * mm, "end": v(126.72, 0.54) * mm});
            skPoint(sketch, "E44.middle", {"position": v(127.9, -1.58) * mm});
            skLineSegment(sketch, "E45.bottom", {"start": v(139.2, -4.08) * mm, "end": v(134.5, -4.08) * mm});
            skLineSegment(sketch, "E45.top", {"start": v(139.2, -3.2) * mm, "end": v(134.5, -3.2) * mm});
            skLineSegment(sketch, "E45.left", {"start": v(139.2, -4.08) * mm, "end": v(139.2, -3.2) * mm});
            skLineSegment(sketch, "E45.right", {"start": v(134.5, -4.08) * mm, "end": v(134.5, -3.2) * mm});
            skPoint(sketch, "E45.middle", {"position": v(136.85, -3.64) * mm});
            skLineSegment(sketch, "E46.bottom", {"start": v(138.66, -1.94) * mm, "end": v(137.45, -1.94) * mm});
            skLineSegment(sketch, "E46.top", {"start": v(138.66, 1.94) * mm, "end": v(137.45, 1.94) * mm});
            skLineSegment(sketch, "E46.left", {"start": v(138.66, -1.94) * mm, "end": v(138.66, 1.94) * mm});
            skLineSegment(sketch, "E46.right", {"start": v(137.45, -1.94) * mm, "end": v(137.45, 1.94) * mm});
            skPoint(sketch, "E46.middle", {"position": v(138.06, 0) * mm});
            skPoint(sketch, "E46.middle.positionSnap0", {"position": v(135.94, 0) * mm});
            skPoint(sketch, "E46.centerSnap0", {"position": v(135.94, 0) * mm});
            skLineSegment(sketch, "E47.bottom", {"start": v(141.54, -1.36) * mm, "end": v(139.87, -1.36) * mm});
            skLineSegment(sketch, "E47.top", {"start": v(141.54, -0.18) * mm, "end": v(139.87, -0.18) * mm});
            skLineSegment(sketch, "E47.left", {"start": v(141.54, -1.36) * mm, "end": v(141.54, -0.18) * mm});
            skLineSegment(sketch, "E47.right", {"start": v(139.87, -1.36) * mm, "end": v(139.87, -0.18) * mm});
            skPoint(sketch, "E47.middle", {"position": v(140.7, -0.77) * mm});
            skLineSegment(sketch, "E48.bottom", {"start": v(162.03, -3.1) * mm, "end": v(161.09, -3.1) * mm});
            skLineSegment(sketch, "E48.top", {"start": v(162.03, 3.1) * mm, "end": v(161.09, 3.1) * mm});
            skLineSegment(sketch, "E48.left", {"start": v(162.03, -3.1) * mm, "end": v(162.03, 3.1) * mm});
            skLineSegment(sketch, "E48.right", {"start": v(161.09, -3.1) * mm, "end": v(161.09, 3.1) * mm});
            skPoint(sketch, "E48.middle", {"position": v(161.56, 0) * mm});
            skLineSegment(sketch, "E49.bottom", {"start": v(158.46, 2.47) * mm, "end": v(146.45, 2.47) * mm});
            skLineSegment(sketch, "E49.top", {"start": v(158.46, 3.65) * mm, "end": v(146.45, 3.65) * mm});
            skLineSegment(sketch, "E49.left", {"start": v(158.46, 2.47) * mm, "end": v(158.46, 3.65) * mm});
            skLineSegment(sketch, "E49.right", {"start": v(146.45, 2.47) * mm, "end": v(146.45, 3.65) * mm});
            skPoint(sketch, "E49.middle", {"position": v(152.45, 3.06) * mm});
            skLineSegment(sketch, "E50.bottom", {"start": v(166.75, -2.25) * mm, "end": v(163.25, -2.25) * mm});
            skLineSegment(sketch, "E50.top", {"start": v(166.75, 1.94) * mm, "end": v(163.25, 1.94) * mm});
            skLineSegment(sketch, "E50.left", {"start": v(166.75, -2.25) * mm, "end": v(166.75, 1.94) * mm});
            skLineSegment(sketch, "E50.right", {"start": v(163.25, -2.25) * mm, "end": v(163.25, 1.94) * mm});
            skPoint(sketch, "E50.middle", {"position": v(165, -0.15) * mm});
            skLineSegment(sketch, "E51.bottom", {"start": v(100.85, -0.29) * mm, "end": v(93.57, -0.29) * mm});
            skLineSegment(sketch, "E51.top", {"start": v(100.85, 0.76) * mm, "end": v(93.57, 0.76) * mm});
            skLineSegment(sketch, "E51.left", {"start": v(100.85, -0.29) * mm, "end": v(100.85, 0.76) * mm});
            skLineSegment(sketch, "E51.right", {"start": v(93.57, -0.29) * mm, "end": v(93.57, 0.76) * mm});
            skPoint(sketch, "E51.middle", {"position": v(97.2, 0.24) * mm});
            skSolve(sketch);
        }
        {
            var Q0;
            {var subQ0=makeQuery(id+"F1.opExtrude","SWEPT_FACE",FACE,{"disambiguationData":[OSD([sQuery(id+"F0.wireOp",EDGE,"E2")])]});Q0=makeQuery(id+"F5.boolean.opBoolean","MERGE",FACE,{"derivedFrom":[subQ0,makeQuery(id+"F5.opPattern","COPY",FACE,{"derivedFrom":subQ0,"instanceName":"1"})]});}
            var sketch = newSketch(context, id + "F16", { "sketchPlane" : qUnion([Q0])});
            skLineSegment(sketch, "E52.bottom", {"start": v(7.94, 3.38) * mm, "end": v(1.14, 3.38) * mm});
            skLineSegment(sketch, "E52.top", {"start": v(7.94, 1.43) * mm, "end": v(1.14, 1.43) * mm});
            skLineSegment(sketch, "E52.left", {"start": v(7.94, 3.38) * mm, "end": v(7.94, 1.43) * mm});
            skLineSegment(sketch, "E52.right", {"start": v(1.14, 3.38) * mm, "end": v(1.14, 1.43) * mm});
            skLineSegment(sketch, "E53.bottom", {"start": v(4.39, -1.43) * mm, "end": v(0, -1.43) * mm});
            skLineSegment(sketch, "E53.top", {"start": v(4.39, -2.93) * mm, "end": v(0, -2.93) * mm});
            skLineSegment(sketch, "E53.left", {"start": v(4.39, -1.43) * mm, "end": v(4.39, -2.93) * mm});
            skLineSegment(sketch, "E53.right", {"start": v(0, -1.43) * mm, "end": v(0, -2.93) * mm});
            skLineSegment(sketch, "E54.bottom", {"start": v(-10.78, 2.03) * mm, "end": v(-2.89, 2.03) * mm});
            skLineSegment(sketch, "E54.top", {"start": v(-10.78, 0) * mm, "end": v(-2.89, 0) * mm});
            skLineSegment(sketch, "E54.left", {"start": v(-10.78, 2.03) * mm, "end": v(-10.78, 0) * mm});
            skLineSegment(sketch, "E54.right", {"start": v(-2.89, 2.03) * mm, "end": v(-2.89, 0) * mm});
            skLineSegment(sketch, "E55.bottom", {"start": v(-9.38, -2.33) * mm, "end": v(-3.35, -2.33) * mm});
            skLineSegment(sketch, "E55.top", {"start": v(-9.38, -3.38) * mm, "end": v(-3.35, -3.38) * mm});
            skLineSegment(sketch, "E55.left", {"start": v(-9.38, -2.33) * mm, "end": v(-9.38, -3.38) * mm});
            skLineSegment(sketch, "E55.right", {"start": v(-3.35, -2.33) * mm, "end": v(-3.35, -3.38) * mm});
            skLineSegment(sketch, "E56.bottom", {"start": v(-20.37, 3.08) * mm, "end": v(-14.64, 3.08) * mm});
            skLineSegment(sketch, "E56.top", {"start": v(-20.37, 1.88) * mm, "end": v(-14.64, 1.88) * mm});
            skLineSegment(sketch, "E56.left", {"start": v(-20.37, 3.08) * mm, "end": v(-20.37, 1.88) * mm});
            skLineSegment(sketch, "E56.right", {"start": v(-14.64, 3.08) * mm, "end": v(-14.64, 1.88) * mm});
            skLineSegment(sketch, "E57.bottom", {"start": v(-19.75, -2.63) * mm, "end": v(-12.94, -2.63) * mm});
            skLineSegment(sketch, "E57.top", {"start": v(-19.75, 0) * mm, "end": v(-12.94, 0) * mm});
            skLineSegment(sketch, "E57.left", {"start": v(-19.75, -2.63) * mm, "end": v(-19.75, 0) * mm});
            skLineSegment(sketch, "E57.right", {"start": v(-12.94, -2.63) * mm, "end": v(-12.94, 0) * mm});
            skPoint(sketch, "E58.firstSnap0", {"position": v(-16.35, 0) * mm});
            skLineSegment(sketch, "E58.bottom", {"start": v(-25.4, 0) * mm, "end": v(-30.97, 0) * mm});
            skLineSegment(sketch, "E58.top", {"start": v(-25.4, 2.03) * mm, "end": v(-30.97, 2.03) * mm});
            skLineSegment(sketch, "E58.left", {"start": v(-25.4, 0) * mm, "end": v(-25.4, 2.03) * mm});
            skLineSegment(sketch, "E58.right", {"start": v(-30.97, 0) * mm, "end": v(-30.97, 2.03) * mm});
            skLineSegment(sketch, "E59.bottom", {"start": v(-24.47, -2.33) * mm, "end": v(-22.15, -2.33) * mm});
            skLineSegment(sketch, "E59.top", {"start": v(-24.47, -3.69) * mm, "end": v(-22.15, -3.69) * mm});
            skLineSegment(sketch, "E59.left", {"start": v(-24.47, -2.33) * mm, "end": v(-24.47, -3.69) * mm});
            skLineSegment(sketch, "E59.right", {"start": v(-22.15, -2.33) * mm, "end": v(-22.15, -3.69) * mm});
            skSolve(sketch);
        }
        {
            var Q0;
            Q0 = qSketchRegion(id + "F16", true);
            extrude(context, id + "F17", {"entities" : qUnion([Q0]), "operationType" : NewBodyOperationType.REMOVE, "oppositeDirection" : true, "depth" : 0.5 * mm});
        }
        {
            var Q0;
            {var subQ0=makeQuery(id+"F1.opExtrude","SWEPT_FACE",FACE,{"disambiguationData":[OSD([sQuery(id+"F0.wireOp",EDGE,"E2")])]});Q0=makeQuery(id+"F5.boolean.opBoolean","MERGE",FACE,{"derivedFrom":[subQ0,makeQuery(id+"F5.opPattern","COPY",FACE,{"derivedFrom":subQ0,"instanceName":"1"})]});}
            var sketch = newSketch(context, id + "F18", { "sketchPlane" : qUnion([Q0])});
            skLineSegment(sketch, "E60.bottom", {"start": v(-31.2, -1.58) * mm, "end": v(-26.87, -1.58) * mm});
            skLineSegment(sketch, "E60.top", {"start": v(-31.2, -3.23) * mm, "end": v(-26.87, -3.23) * mm});
            skLineSegment(sketch, "E60.left", {"start": v(-31.2, -1.58) * mm, "end": v(-31.2, -3.23) * mm});
            skLineSegment(sketch, "E60.right", {"start": v(-26.87, -1.58) * mm, "end": v(-26.87, -3.23) * mm});
            skLineSegment(sketch, "E61.bottom", {"start": v(-39.24, -0.38) * mm, "end": v(-33.98, -0.38) * mm});
            skLineSegment(sketch, "E61.top", {"start": v(-39.24, -2.63) * mm, "end": v(-33.98, -2.63) * mm});
            skLineSegment(sketch, "E61.left", {"start": v(-39.24, -0.38) * mm, "end": v(-39.24, -2.63) * mm});
            skLineSegment(sketch, "E61.right", {"start": v(-33.98, -0.38) * mm, "end": v(-33.98, -2.63) * mm});
            skLineSegment(sketch, "E62.bottom", {"start": v(-40.33, 3.08) * mm, "end": v(-34.91, 3.08) * mm});
            skLineSegment(sketch, "E62.top", {"start": v(-40.33, 1.58) * mm, "end": v(-34.91, 1.58) * mm});
            skLineSegment(sketch, "E62.left", {"start": v(-40.33, 3.08) * mm, "end": v(-40.33, 1.58) * mm});
            skLineSegment(sketch, "E62.right", {"start": v(-34.91, 3.08) * mm, "end": v(-34.91, 1.58) * mm});
            skLineSegment(sketch, "E63.bottom", {"start": v(-45.9, -3.38) * mm, "end": v(-40.94, -3.38) * mm});
            skLineSegment(sketch, "E63.top", {"start": v(-45.9, -1.88) * mm, "end": v(-40.94, -1.88) * mm});
            skLineSegment(sketch, "E63.left", {"start": v(-45.9, -3.38) * mm, "end": v(-45.9, -1.88) * mm});
            skLineSegment(sketch, "E63.right", {"start": v(-40.94, -3.38) * mm, "end": v(-40.94, -1.88) * mm});
            skLineSegment(sketch, "E64.bottom", {"start": v(-49.6, 2.03) * mm, "end": v(-43.42, 2.03) * mm});
            skLineSegment(sketch, "E64.top", {"start": v(-49.6, 0) * mm, "end": v(-43.42, 0) * mm});
            skLineSegment(sketch, "E64.left", {"start": v(-49.6, 2.03) * mm, "end": v(-49.6, 0) * mm});
            skLineSegment(sketch, "E64.right", {"start": v(-43.42, 2.03) * mm, "end": v(-43.42, 0) * mm});
            skLineSegment(sketch, "E65.bottom", {"start": v(-56.41, -1.88) * mm, "end": v(-50.38, -1.88) * mm});
            skLineSegment(sketch, "E65.top", {"start": v(-56.41, -3.69) * mm, "end": v(-50.38, -3.69) * mm});
            skLineSegment(sketch, "E65.left", {"start": v(-56.41, -1.88) * mm, "end": v(-56.41, -3.69) * mm});
            skLineSegment(sketch, "E65.right", {"start": v(-50.38, -1.88) * mm, "end": v(-50.38, -3.69) * mm});
            skLineSegment(sketch, "E66.bottom", {"start": v(-60.75, 3.54) * mm, "end": v(-51.46, 3.54) * mm});
            skLineSegment(sketch, "E66.top", {"start": v(-60.75, 1.43) * mm, "end": v(-51.46, 1.43) * mm});
            skLineSegment(sketch, "E66.left", {"start": v(-60.75, 3.54) * mm, "end": v(-60.75, 1.43) * mm});
            skLineSegment(sketch, "E66.right", {"start": v(-51.46, 3.54) * mm, "end": v(-51.46, 1.43) * mm});
            skLineSegment(sketch, "E67.bottom", {"start": v(-62.45, -1.43) * mm, "end": v(-59.5, -1.43) * mm});
            skLineSegment(sketch, "E67.top", {"start": v(-62.45, -3.23) * mm, "end": v(-59.5, -3.23) * mm});
            skLineSegment(sketch, "E67.left", {"start": v(-62.45, -1.43) * mm, "end": v(-62.45, -3.23) * mm});
            skLineSegment(sketch, "E67.right", {"start": v(-59.5, -1.43) * mm, "end": v(-59.5, -3.23) * mm});
            skLineSegment(sketch, "E68.bottom", {"start": v(-70.03, 2.48) * mm, "end": v(-64.92, 2.48) * mm});
            skLineSegment(sketch, "E68.top", {"start": v(-70.03, 0) * mm, "end": v(-64.92, 0) * mm});
            skLineSegment(sketch, "E68.left", {"start": v(-70.03, 2.48) * mm, "end": v(-70.03, 0) * mm});
            skLineSegment(sketch, "E68.right", {"start": v(-64.92, 2.48) * mm, "end": v(-64.92, 0) * mm});
            skSolve(sketch);
        }
        {
            var Q0;
            Q0 = qSketchRegion(id + "F18", true);
            extrude(context, id + "F19", {"entities" : qUnion([Q0]), "operationType" : NewBodyOperationType.REMOVE, "oppositeDirection" : true, "depth" : 0.5 * mm});
        }
        {
            var Q0;
            Q0=qCreatedBy(makeId("Top.planeOp"),FACE);
            cPlane(context, id + "F20", {"entities" : qUnion([Q0]), "cplaneType" : CPlaneType.OFFSET, "offset" : 10 * mm, "oppositeDirection" : true, "width" : 150 * mm, "height" : 150 * mm});
        }
        {
            var Q0;
            Q0=qCreatedBy(id+"F20.planeOp",FACE);
            var sketch = newSketch(context, id + "F21", { "sketchPlane" : qUnion([Q0])});
            skArc(sketch, "E69", {"start": v(0, 12.05) * mm, "mid": v(-12.05, 0) * mm, "end": v(0, -12.05) * mm});
            skLineSegment(sketch, "E70", {"start": v(0, 12.05) * mm, "end": v(0, -12.05) * mm});
            skSolve(sketch);
        }
        {
            var Q0;
            Q0 = qSketchRegion(id + "F21", true);
            var Q1;
            Q1=sQuery(id+"F21.wireOp",EDGE,"E70");
            revolve(context, id + "F22", {"operationType" : NewBodyOperationType.ADD, "entities" : qUnion([Q0]), "axis" : qUnion([Q1]), "revolveType" : RevolveType.FULL});
        }
        {
            var Q0;
            {var subQ0=makeQuery(id+"F1.opExtrude","SWEPT_FACE",FACE,{"disambiguationData":[OSD([sQuery(id+"F0.wireOp",EDGE,"E2")])]});Q0=makeQuery(id+"F5.boolean.opBoolean","MERGE",FACE,{"derivedFrom":[subQ0,makeQuery(id+"F5.opPattern","COPY",FACE,{"derivedFrom":subQ0,"instanceName":"1"})]});}
            var sketch = newSketch(context, id + "F23", { "sketchPlane" : qUnion([Q0])});
            skLineSegment(sketch, "E71.bottom", {"start": v(-70.03, -3.38) * mm, "end": v(-64.3, -3.38) * mm});
            skLineSegment(sketch, "E71.top", {"start": v(-70.03, -1.43) * mm, "end": v(-64.3, -1.43) * mm});
            skLineSegment(sketch, "E71.left", {"start": v(-70.03, -3.38) * mm, "end": v(-70.03, -1.43) * mm});
            skLineSegment(sketch, "E71.right", {"start": v(-64.3, -3.38) * mm, "end": v(-64.3, -1.43) * mm});
            skLineSegment(sketch, "E72.bottom", {"start": v(-76.06, 3.54) * mm, "end": v(-71.89, 3.54) * mm});
            skLineSegment(sketch, "E72.top", {"start": v(-76.06, 0) * mm, "end": v(-71.89, 0) * mm});
            skLineSegment(sketch, "E72.left", {"start": v(-76.06, 3.54) * mm, "end": v(-76.06, 0) * mm});
            skLineSegment(sketch, "E72.right", {"start": v(-71.89, 3.54) * mm, "end": v(-71.89, 0) * mm});
            skLineSegment(sketch, "E73.bottom", {"start": v(-81.17, -2.33) * mm, "end": v(-73.74, -2.33) * mm});
            skLineSegment(sketch, "E73.top", {"start": v(-81.17, -3.69) * mm, "end": v(-73.74, -3.69) * mm});
            skLineSegment(sketch, "E73.left", {"start": v(-81.17, -2.33) * mm, "end": v(-81.17, -3.69) * mm});
            skLineSegment(sketch, "E73.right", {"start": v(-73.74, -2.33) * mm, "end": v(-73.74, -3.69) * mm});
            skPoint(sketch, "E74.oppositeSnap0", {"position": v(-76.06, 1.77) * mm});
            skLineSegment(sketch, "E74.bottom", {"start": v(-81.17, 0) * mm, "end": v(-77.46, 0) * mm});
            skLineSegment(sketch, "E74.top", {"start": v(-81.17, 1.77) * mm, "end": v(-77.46, 1.77) * mm});
            skLineSegment(sketch, "E74.left", {"start": v(-81.17, 0) * mm, "end": v(-81.17, 1.77) * mm});
            skLineSegment(sketch, "E74.right", {"start": v(-77.46, 0) * mm, "end": v(-77.46, 1.77) * mm});
            skLineSegment(sketch, "E75.bottom", {"start": v(-87.82, -1.88) * mm, "end": v(-83.02, -1.88) * mm});
            skLineSegment(sketch, "E75.top", {"start": v(-87.82, -2.93) * mm, "end": v(-83.02, -2.93) * mm});
            skLineSegment(sketch, "E75.left", {"start": v(-87.82, -1.88) * mm, "end": v(-87.82, -2.93) * mm});
            skLineSegment(sketch, "E75.right", {"start": v(-83.02, -1.88) * mm, "end": v(-83.02, -2.93) * mm});
            skLineSegment(sketch, "E76.bottom", {"start": v(-89.37, 3.84) * mm, "end": v(-83.02, 3.84) * mm});
            skLineSegment(sketch, "E76.top", {"start": v(-89.37, 1.73) * mm, "end": v(-83.02, 1.73) * mm});
            skLineSegment(sketch, "E76.left", {"start": v(-89.37, 3.84) * mm, "end": v(-89.37, 1.73) * mm});
            skLineSegment(sketch, "E76.right", {"start": v(-83.02, 3.84) * mm, "end": v(-83.02, 1.73) * mm});
            skLineSegment(sketch, "E77.bottom", {"start": v(-95.56, 0) * mm, "end": v(-92.46, 0) * mm});
            skLineSegment(sketch, "E77.top", {"start": v(-95.56, -1.88) * mm, "end": v(-92.46, -1.88) * mm});
            skLineSegment(sketch, "E77.left", {"start": v(-95.56, 0) * mm, "end": v(-95.56, -1.88) * mm});
            skLineSegment(sketch, "E77.right", {"start": v(-92.46, 0) * mm, "end": v(-92.46, -1.88) * mm});
            skLineSegment(sketch, "E78.bottom", {"start": v(-104.37, -1.88) * mm, "end": v(-99.11, -1.88) * mm});
            skLineSegment(sketch, "E78.top", {"start": v(-104.37, -3.69) * mm, "end": v(-99.11, -3.69) * mm});
            skLineSegment(sketch, "E78.left", {"start": v(-104.37, -1.88) * mm, "end": v(-104.37, -3.69) * mm});
            skLineSegment(sketch, "E78.right", {"start": v(-99.11, -1.88) * mm, "end": v(-99.11, -3.69) * mm});
            skLineSegment(sketch, "E79.bottom", {"start": v(-95.87, 2.93) * mm, "end": v(-90.91, 2.93) * mm});
            skLineSegment(sketch, "E79.top", {"start": v(-95.87, 1.73) * mm, "end": v(-90.91, 1.73) * mm});
            skLineSegment(sketch, "E79.left", {"start": v(-95.87, 2.93) * mm, "end": v(-95.87, 1.73) * mm});
            skLineSegment(sketch, "E79.right", {"start": v(-90.91, 2.93) * mm, "end": v(-90.91, 1.73) * mm});
            skLineSegment(sketch, "E80.bottom", {"start": v(-102.67, 0) * mm, "end": v(-99.89, 0) * mm});
            skLineSegment(sketch, "E80.top", {"start": v(-102.67, 1.73) * mm, "end": v(-99.89, 1.73) * mm});
            skLineSegment(sketch, "E80.left", {"start": v(-102.67, 0) * mm, "end": v(-102.67, 1.73) * mm});
            skLineSegment(sketch, "E80.right", {"start": v(-99.89, 0) * mm, "end": v(-99.89, 1.73) * mm});
            skSolve(sketch);
        }
        {
            var Q0;
            Q0 = qSketchRegion(id + "F23", true);
            extrude(context, id + "F24", {"entities" : qUnion([Q0]), "operationType" : NewBodyOperationType.REMOVE, "oppositeDirection" : true, "depth" : 0.5 * mm});
        }
        {
            var Q0;
            {var subQ0=makeQuery(id+"F1.opExtrude","SWEPT_FACE",FACE,{"disambiguationData":[OSD([sQuery(id+"F0.wireOp",EDGE,"E2")])]});Q0=makeQuery(id+"F5.boolean.opBoolean","MERGE",FACE,{"derivedFrom":[subQ0,makeQuery(id+"F5.opPattern","COPY",FACE,{"derivedFrom":subQ0,"instanceName":"1"})]});}
            var sketch = newSketch(context, id + "F25", { "sketchPlane" : qUnion([Q0])});
            skLineSegment(sketch, "E81.bottom", {"start": v(-107.93, 2.03) * mm, "end": v(-104.68, 2.03) * mm});
            skLineSegment(sketch, "E81.top", {"start": v(-107.93, 0) * mm, "end": v(-104.68, 0) * mm});
            skLineSegment(sketch, "E81.left", {"start": v(-107.93, 2.03) * mm, "end": v(-107.93, 0) * mm});
            skLineSegment(sketch, "E81.right", {"start": v(-104.68, 2.03) * mm, "end": v(-104.68, 0) * mm});
            skLineSegment(sketch, "E82.bottom", {"start": v(-109.79, -3.54) * mm, "end": v(-106.23, -3.54) * mm});
            skLineSegment(sketch, "E82.top", {"start": v(-109.79, -2.48) * mm, "end": v(-106.23, -2.48) * mm});
            skLineSegment(sketch, "E82.left", {"start": v(-109.79, -3.54) * mm, "end": v(-109.79, -2.48) * mm});
            skLineSegment(sketch, "E82.right", {"start": v(-106.23, -3.54) * mm, "end": v(-106.23, -2.48) * mm});
            skLineSegment(sketch, "E83.bottom", {"start": v(-113.2, 3.38) * mm, "end": v(-109.33, 3.38) * mm});
            skLineSegment(sketch, "E83.top", {"start": v(-113.2, 2.03) * mm, "end": v(-109.33, 2.03) * mm});
            skLineSegment(sketch, "E83.left", {"start": v(-113.2, 3.38) * mm, "end": v(-113.2, 2.03) * mm});
            skLineSegment(sketch, "E83.right", {"start": v(-109.33, 3.38) * mm, "end": v(-109.33, 2.03) * mm});
            skLineSegment(sketch, "E84.bottom", {"start": v(-119.38, -1.88) * mm, "end": v(-112.26, -1.88) * mm});
            skLineSegment(sketch, "E84.top", {"start": v(-119.38, -2.63) * mm, "end": v(-112.26, -2.63) * mm});
            skLineSegment(sketch, "E84.left", {"start": v(-119.38, -1.88) * mm, "end": v(-119.38, -2.63) * mm});
            skLineSegment(sketch, "E84.right", {"start": v(-112.26, -1.88) * mm, "end": v(-112.26, -2.63) * mm});
            skLineSegment(sketch, "E85.bottom", {"start": v(-120, 1.58) * mm, "end": v(-115.2, 1.58) * mm});
            skLineSegment(sketch, "E85.top", {"start": v(-120, 0) * mm, "end": v(-115.2, 0) * mm});
            skLineSegment(sketch, "E85.left", {"start": v(-120, 1.58) * mm, "end": v(-120, 0) * mm});
            skLineSegment(sketch, "E85.right", {"start": v(-115.2, 1.58) * mm, "end": v(-115.2, 0) * mm});
            skLineSegment(sketch, "E86.bottom", {"start": v(-123.87, -2.18) * mm, "end": v(-130.06, -2.18) * mm});
            skLineSegment(sketch, "E86.top", {"start": v(-123.87, 0) * mm, "end": v(-130.06, 0) * mm});
            skLineSegment(sketch, "E86.left", {"start": v(-123.87, -2.18) * mm, "end": v(-123.87, 0) * mm});
            skLineSegment(sketch, "E86.right", {"start": v(-130.06, -2.18) * mm, "end": v(-130.06, 0) * mm});
            skLineSegment(sketch, "E87.bottom", {"start": v(-126.5, 3.08) * mm, "end": v(-121.86, 3.08) * mm});
            skLineSegment(sketch, "E87.top", {"start": v(-126.5, 1.43) * mm, "end": v(-121.86, 1.43) * mm});
            skLineSegment(sketch, "E87.left", {"start": v(-126.5, 3.08) * mm, "end": v(-126.5, 1.43) * mm});
            skLineSegment(sketch, "E87.right", {"start": v(-121.86, 3.08) * mm, "end": v(-121.86, 1.43) * mm});
            skLineSegment(sketch, "E88.bottom", {"start": v(-136.55, -3.69) * mm, "end": v(-132.69, -3.69) * mm});
            skLineSegment(sketch, "E88.top", {"start": v(-136.55, -2.18) * mm, "end": v(-132.69, -2.18) * mm});
            skLineSegment(sketch, "E88.left", {"start": v(-136.55, -3.69) * mm, "end": v(-136.55, -2.18) * mm});
            skLineSegment(sketch, "E88.right", {"start": v(-132.69, -3.69) * mm, "end": v(-132.69, -2.18) * mm});
            skLineSegment(sketch, "E89.bottom", {"start": v(-135.47, 3.54) * mm, "end": v(-130.06, 3.54) * mm});
            skLineSegment(sketch, "E89.top", {"start": v(-135.47, 1.58) * mm, "end": v(-130.06, 1.58) * mm});
            skLineSegment(sketch, "E89.left", {"start": v(-135.47, 3.54) * mm, "end": v(-135.47, 1.58) * mm});
            skLineSegment(sketch, "E89.right", {"start": v(-130.06, 3.54) * mm, "end": v(-130.06, 1.58) * mm});
            skLineSegment(sketch, "E90.bottom", {"start": v(-141.5, 1.73) * mm, "end": v(-138.57, 1.73) * mm});
            skLineSegment(sketch, "E90.top", {"start": v(-141.5, -2.18) * mm, "end": v(-138.57, -2.18) * mm});
            skLineSegment(sketch, "E90.left", {"start": v(-141.5, 1.73) * mm, "end": v(-141.5, -2.18) * mm});
            skLineSegment(sketch, "E90.right", {"start": v(-138.57, 1.73) * mm, "end": v(-138.57, -2.18) * mm});
            skLineSegment(sketch, "E91.bottom", {"start": v(-147.85, 2.78) * mm, "end": v(-146.6, 2.78) * mm});
            skLineSegment(sketch, "E91.top", {"start": v(-147.85, -2.18) * mm, "end": v(-146.6, -2.18) * mm});
            skLineSegment(sketch, "E91.left", {"start": v(-147.85, 2.78) * mm, "end": v(-147.85, -2.18) * mm});
            skLineSegment(sketch, "E91.right", {"start": v(-146.6, 2.78) * mm, "end": v(-146.6, -2.18) * mm});
            skLineSegment(sketch, "E92.bottom", {"start": v(-144.13, 0) * mm, "end": v(-143.05, 0) * mm});
            skLineSegment(sketch, "E92.top", {"start": v(-144.13, -1.58) * mm, "end": v(-143.05, -1.58) * mm});
            skLineSegment(sketch, "E92.left", {"start": v(-144.13, 0) * mm, "end": v(-144.13, -1.58) * mm});
            skLineSegment(sketch, "E92.right", {"start": v(-143.05, 0) * mm, "end": v(-143.05, -1.58) * mm});
            skLineSegment(sketch, "E93.bottom", {"start": v(-154.65, 2.48) * mm, "end": v(-150.32, 2.48) * mm});
            skLineSegment(sketch, "E93.top", {"start": v(-154.65, 1.43) * mm, "end": v(-150.32, 1.43) * mm});
            skLineSegment(sketch, "E93.left", {"start": v(-154.65, 2.48) * mm, "end": v(-154.65, 1.43) * mm});
            skLineSegment(sketch, "E93.right", {"start": v(-150.32, 2.48) * mm, "end": v(-150.32, 1.43) * mm});
            skLineSegment(sketch, "E94.bottom", {"start": v(-154.2, -3.08) * mm, "end": v(-150.32, -3.08) * mm});
            skLineSegment(sketch, "E94.top", {"start": v(-154.2, 0) * mm, "end": v(-150.32, 0) * mm});
            skLineSegment(sketch, "E94.left", {"start": v(-154.2, -3.08) * mm, "end": v(-154.2, 0) * mm});
            skLineSegment(sketch, "E94.right", {"start": v(-150.32, -3.08) * mm, "end": v(-150.32, 0) * mm});
            skLineSegment(sketch, "E95.bottom", {"start": v(-161, 2.93) * mm, "end": v(-158.99, 2.93) * mm});
            skLineSegment(sketch, "E95.top", {"start": v(-161, 0) * mm, "end": v(-158.99, 0) * mm});
            skLineSegment(sketch, "E95.left", {"start": v(-161, 2.93) * mm, "end": v(-161, 0) * mm});
            skLineSegment(sketch, "E95.right", {"start": v(-158.99, 2.93) * mm, "end": v(-158.99, 0) * mm});
            skLineSegment(sketch, "E96.bottom", {"start": v(-158.06, -2.18) * mm, "end": v(-154.2, -2.18) * mm});
            skLineSegment(sketch, "E96.top", {"start": v(-158.06, -3.08) * mm, "end": v(-154.2, -3.08) * mm});
            skLineSegment(sketch, "E96.left", {"start": v(-158.06, -2.18) * mm, "end": v(-158.06, -3.08) * mm});
            skLineSegment(sketch, "E96.right", {"start": v(-154.2, -2.18) * mm, "end": v(-154.2, -3.08) * mm});
            skSolve(sketch);
        }
        {
            var Q0;
            Q0 = qSketchRegion(id + "F25", true);
            extrude(context, id + "F26", {"entities" : qUnion([Q0]), "operationType" : NewBodyOperationType.REMOVE, "oppositeDirection" : true, "depth" : 0.5 * mm});
        }
        {
            var Q0;
            Q0=makeQuery(id+"F4.opLoft","SWEPT_FACE",FACE,{"disambiguationData":[OSD([sQuery(id+"F0.wireOp",EDGE,"E1"),sQuery(id+"F0.wireOp",EDGE,"E2"),sQuery(id+"F0.wireOp",EDGE,"E3")])]});
            var sketch = newSketch(context, id + "F27", { "sketchPlane" : qUnion([Q0])});
            skPoint(sketch, "E97.end.orphan", {"position": v(0, 25.31) * mm});
            skLineSegment(sketch, "E98", {"start": v(-12.5, -4.87) * mm, "end": v(-13.01, 21.95) * mm});
            skLineSegment(sketch, "E99", {"start": v(-13.01, 21.95) * mm, "end": v(10.33, 22.4) * mm});
            skLineSegment(sketch, "E100", {"start": v(10.33, 22.4) * mm, "end": v(10.5, 13.07) * mm});
            skLineSegment(sketch, "E101", {"start": v(10.5, 13.07) * mm, "end": v(46.2, 13.74) * mm});
            skLineSegment(sketch, "E102", {"start": v(46.2, 13.74) * mm, "end": v(46.54, -3.75) * mm});
            skLineSegment(sketch, "E103", {"start": v(46.54, -3.75) * mm, "end": v(-12.5, -4.87) * mm});
            skSolve(sketch);
        }
        {
            var Q0;
            Q0 = qSketchRegion(id + "F27", true);
            extrude(context, id + "F28", {"entities" : qUnion([Q0]), "operationType" : NewBodyOperationType.ADD, "depth" : 3 * mm});
        }
        {
            var Q0;
            Q0=makeQuery(id+"F28.opExtrude","CAP_EDGE",EDGE,{"disambiguationData":[OSD([sQuery(id+"F27.wireOp",EDGE,"E98")])],"isStart":false});
            var Q1;
            Q1=makeQuery(id+"F28.opExtrude","CAP_EDGE",EDGE,{"disambiguationData":[OSD([sQuery(id+"F27.wireOp",EDGE,"E99")])],"isStart":false});
            var Q2;
            Q2=makeQuery(id+"F28.opExtrude","CAP_EDGE",EDGE,{"disambiguationData":[OSD([sQuery(id+"F27.wireOp",EDGE,"E100")])],"isStart":false});
            var Q3;
            Q3=makeQuery(id+"F28.opExtrude","CAP_EDGE",EDGE,{"disambiguationData":[OSD([sQuery(id+"F27.wireOp",EDGE,"Fqhbjiei-WFTk-KmZo-Y0PG-tCrZUfIXa4XS")])],"isStart":false});
            var Q4;
            Q4=makeQuery(id+"F28.opExtrude","CAP_EDGE",EDGE,{"disambiguationData":[OSD([sQuery(id+"F27.wireOp",EDGE,"263AYR1b-NvKc-OPJP-V27c-pHVCoOBViCw9")])],"isStart":false});
            var Q5;
            Q5=makeQuery(id+"F28.opExtrude","CAP_EDGE",EDGE,{"disambiguationData":[OSD([sQuery(id+"F27.wireOp",EDGE,"E101")])],"isStart":false});
            var Q6;
            Q6=makeQuery(id+"F28.opExtrude","CAP_EDGE",EDGE,{"disambiguationData":[OSD([sQuery(id+"F27.wireOp",EDGE,"E102")])],"isStart":false});
            chamfer(context, id + "F29", {"entities" : qUnion([Q0, Q1, Q2, Q3, Q4, Q5, Q6]), "width" : 1 * mm, "tangentPropagation" : true});
        }
        {
            var Q0;
            Q0=makeQuery(id+"F1.opExtrude","SWEPT_BODY",BODY,{"disambiguationData":[OSD([sQuery(id+"F0.wireOp",EDGE,"E0"),sQuery(id+"F0.wireOp",EDGE,"E1"),sQuery(id+"F0.wireOp",EDGE,"E2"),sQuery(id+"F0.wireOp",EDGE,"E3")])]});
            var Q1;
            Q1=qCreatedBy(makeId("Front.planeOp"),FACE);
            mirror(context, id + "F30", {"operationType" : NewBodyOperationType.ADD, "entities" : qUnion([Q0]), "mirrorPlane" : qUnion([Q1])});
        }
        {
            var Q0;
            Q0=makeQuery(id+"F4.opLoft","SWEPT_FACE",FACE,{"disambiguationData":[OSD([sQuery(id+"F0.wireOp",EDGE,"E1"),sQuery(id+"F0.wireOp",EDGE,"E2"),sQuery(id+"F0.wireOp",EDGE,"E3")])]});
            var sketch = newSketch(context, id + "F31", { "sketchPlane" : qUnion([Q0])});
            skPoint(sketch, "E104.oppositeSnap0", {"position": v(10.42, 17.73) * mm});
            skLineSegment(sketch, "E104.bottom", {"start": v(-12.5, -4.87) * mm, "end": v(33.57, -4.87) * mm});
            skLineSegment(sketch, "E104.top", {"start": v(-12.5, 17.73) * mm, "end": v(33.57, 17.73) * mm});
            skLineSegment(sketch, "E104.left", {"start": v(-12.5, -4.87) * mm, "end": v(-12.5, 17.73) * mm});
            skLineSegment(sketch, "E104.right", {"start": v(33.57, -4.87) * mm, "end": v(33.57, 17.73) * mm});
            skSolve(sketch);
        }
        {
            var Q0;
            Q0 = qSketchRegion(id + "F31", true);
            extrude(context, id + "F32", {"entities" : qUnion([Q0]), "operationType" : NewBodyOperationType.ADD, "depth" : 7 * mm});
        }
        {
            var Q0;
            Q0=makeQuery(id+"F32.opExtrude","CAP_EDGE",EDGE,{"disambiguationData":[OSD([sQuery(id+"F31.wireOp",EDGE,"E104.left")])],"isStart":false});
            var Q1;
            Q1=makeQuery(id+"F32.opExtrude","CAP_EDGE",EDGE,{"disambiguationData":[OSD([sQuery(id+"F31.wireOp",EDGE,"E104.top")])],"isStart":false});
            var Q2;
            Q2=makeQuery(id+"F32.opExtrude","CAP_EDGE",EDGE,{"disambiguationData":[OSD([sQuery(id+"F31.wireOp",EDGE,"E104.right")])],"isStart":false});
            chamfer(context, id + "F33", {"entities" : qUnion([Q0, Q1, Q2]), "width" : 1 * mm, "tangentPropagation" : true});
        }
        {
            var Q0;
            Q0=makeQuery(id+"F1.opExtrude","SWEPT_BODY",BODY,{"disambiguationData":[OSD([sQuery(id+"F0.wireOp",EDGE,"E0"),sQuery(id+"F0.wireOp",EDGE,"E1"),sQuery(id+"F0.wireOp",EDGE,"E2"),sQuery(id+"F0.wireOp",EDGE,"E3")])]});
            var Q1;
            Q1=qCreatedBy(makeId("Front.planeOp"),FACE);
            mirror(context, id + "F34", {"operationType" : NewBodyOperationType.ADD, "entities" : qUnion([Q0]), "mirrorPlane" : qUnion([Q1])});
        }
        {
            var Q0;
            Q0=makeQuery(id+"F32.opExtrude","CAP_FACE",FACE,{"disambiguationData":[OSD([sQuery(id+"F31.wireOp",EDGE,"E104.bottom"),sQuery(id+"F31.wireOp",EDGE,"E104.top"),sQuery(id+"F31.wireOp",EDGE,"E104.left"),sQuery(id+"F31.wireOp",EDGE,"E104.right")])],"isStart":false});
            var sketch = newSketch(context, id + "F35", { "sketchPlane" : qUnion([Q0])});
            skLineSegment(sketch, "E105.bottom", {"start": v(-11.5, -4.87) * mm, "end": v(18.35, -4.87) * mm});
            skLineSegment(sketch, "E105.top", {"start": v(-11.5, 10.65) * mm, "end": v(18.35, 10.65) * mm});
            skLineSegment(sketch, "E105.left", {"start": v(-11.5, -4.87) * mm, "end": v(-11.5, 10.65) * mm});
            skLineSegment(sketch, "E105.right", {"start": v(18.35, -4.87) * mm, "end": v(18.35, 10.65) * mm});
            skSolve(sketch);
        }
        {
            var Q0;
            Q0 = qSketchRegion(id + "F35", true);
            extrude(context, id + "F36", {"entities" : qUnion([Q0]), "operationType" : NewBodyOperationType.ADD, "depth" : 4 * mm});
        }
        {
            var Q0;
            Q0=makeQuery(id+"F36.opExtrude","CAP_EDGE",EDGE,{"disambiguationData":[OSD([sQuery(id+"F35.wireOp",EDGE,"E105.left")])],"isStart":false});
            var Q1;
            Q1=makeQuery(id+"F36.opExtrude","CAP_EDGE",EDGE,{"disambiguationData":[OSD([sQuery(id+"F35.wireOp",EDGE,"E105.top")])],"isStart":false});
            var Q2;
            Q2=makeQuery(id+"F36.opExtrude","CAP_EDGE",EDGE,{"disambiguationData":[OSD([sQuery(id+"F35.wireOp",EDGE,"E105.right")])],"isStart":false});
            chamfer(context, id + "F37", {"entities" : qUnion([Q0, Q1, Q2]), "width" : 1 * mm, "tangentPropagation" : true});
        }
        {
            var Q0;
            Q0=makeQuery(id+"F1.opExtrude","SWEPT_BODY",BODY,{"disambiguationData":[OSD([sQuery(id+"F0.wireOp",EDGE,"E0"),sQuery(id+"F0.wireOp",EDGE,"E1"),sQuery(id+"F0.wireOp",EDGE,"E2"),sQuery(id+"F0.wireOp",EDGE,"E3")])]});
            var Q1;
            Q1=qCreatedBy(makeId("Front.planeOp"),FACE);
            mirror(context, id + "F38", {"operationType" : NewBodyOperationType.ADD, "entities" : qUnion([Q0]), "mirrorPlane" : qUnion([Q1])});
        }
        {
            var Q0;
            Q0=qCreatedBy(makeId("Top.planeOp"),FACE);
            cPlane(context, id + "F39", {"entities" : qUnion([Q0]), "cplaneType" : CPlaneType.OFFSET, "offset" : 8 * mm, "width" : 150 * mm, "height" : 150 * mm});
        }
        {
            var Q0;
            Q0=qCreatedBy(id+"F39.planeOp",FACE);
            cPlane(context, id + "F40", {"entities" : qUnion([Q0]), "cplaneType" : CPlaneType.OFFSET, "offset" : 30 * mm, "width" : 150 * mm, "height" : 150 * mm});
        }
        {
            var Q0;
            Q0=qCreatedBy(id+"F39.planeOp",FACE);
            var sketch = newSketch(context, id + "F41", { "sketchPlane" : qUnion([Q0])});
            skLineSegment(sketch, "E106.bottom", {"start": v(-23.13, -9.92) * mm, "end": v(23.13, -9.92) * mm});
            skLineSegment(sketch, "E106.top", {"start": v(-23.13, 9.92) * mm, "end": v(23.13, 9.92) * mm});
            skLineSegment(sketch, "E106.left", {"start": v(-23.13, -9.92) * mm, "end": v(-23.13, 9.92) * mm});
            skLineSegment(sketch, "E106.right", {"start": v(23.13, -9.92) * mm, "end": v(23.13, 9.92) * mm});
            skPoint(sketch, "E106.middle", {"position": v(0, 0) * mm});
            skSolve(sketch);
        }
        {
            var Q0;
            Q0=qCreatedBy(id+"F40.planeOp",FACE);
            var sketch = newSketch(context, id + "F42", { "sketchPlane" : qUnion([Q0])});
            skLineSegment(sketch, "E107.bottom", {"start": v(-7.17, -4.36) * mm, "end": v(7.17, -4.36) * mm});
            skLineSegment(sketch, "E107.top", {"start": v(-7.17, 4.36) * mm, "end": v(7.17, 4.36) * mm});
            skLineSegment(sketch, "E107.left", {"start": v(-7.17, -4.36) * mm, "end": v(-7.17, 4.36) * mm});
            skLineSegment(sketch, "E107.right", {"start": v(7.17, -4.36) * mm, "end": v(7.17, 4.36) * mm});
            skPoint(sketch, "E107.middle", {"position": v(0, 0) * mm});
            skSolve(sketch);
        }
        {
            var Q1;
            Q1 = qSketchRegion(id + "F42", true);
            var Q2;
            Q2 = qSketchRegion(id + "F41", true);
            loft(context, id + "F43", {"operationType" : NewBodyOperationType.ADD, "sheetProfilesArray" : [{ "sheetProfileEntities" : qUnion([Q1]) }, { "sheetProfileEntities" : qUnion([Q2]) }]});
        }
        {
            var Q1;
            Q1=makeQuery(id+"F36.boolean.opBoolean","MERGE",FACE,{"derivedFrom":[makeQuery(id+"F32.opExtrude","SWEPT_FACE",FACE,{"disambiguationData":[OSD([sQuery(id+"F31.wireOp",EDGE,"E104.bottom")])]}),makeQuery(id+"F36.opExtrude","SWEPT_FACE",FACE,{"disambiguationData":[OSD([sQuery(id+"F35.wireOp",EDGE,"E105.bottom")])]})]});
            var Q2;
            {var subQ0=makeQuery(id+"F32.opExtrude","SWEPT_FACE",FACE,{"disambiguationData":[OSD([sQuery(id+"F31.wireOp",EDGE,"E104.bottom")])]});Q2=makeQuery(id+"F38.boolean.opBoolean","MERGE",FACE,{"derivedFrom":[makeQuery(id+"F34.opPattern","COPY",FACE,{"derivedFrom":subQ0,"instanceName":"1"}),makeQuery(id+"F38.opPattern","COPY",FACE,{"derivedFrom":makeQuery(id+"F36.boolean.opBoolean","MERGE",FACE,{"derivedFrom":[subQ0,makeQuery(id+"F36.opExtrude","SWEPT_FACE",FACE,{"disambiguationData":[OSD([sQuery(id+"F35.wireOp",EDGE,"E105.bottom")])]})]}),"instanceName":"1"})]});}
            loft(context, id + "F44", {"operationType" : NewBodyOperationType.ADD, "sheetProfilesArray" : [{ "sheetProfileEntities" : qUnion([Q1]) }, { "sheetProfileEntities" : qUnion([Q2]) }]});
        }
        {
            var Q1;
            Q1=makeQuery(id+"F30.opPattern","COPY",FACE,{"derivedFrom":makeQuery(id+"F28.opExtrude","SWEPT_FACE",FACE,{"disambiguationData":[OSD([sQuery(id+"F27.wireOp",EDGE,"E103")])]}),"instanceName":"1"});
            var Q2;
            Q2=makeQuery(id+"F28.opExtrude","SWEPT_FACE",FACE,{"disambiguationData":[OSD([sQuery(id+"F27.wireOp",EDGE,"E103")])]});
            loft(context, id + "F45", {"operationType" : NewBodyOperationType.ADD, "sheetProfilesArray" : [{ "sheetProfileEntities" : qUnion([Q1]) }, { "sheetProfileEntities" : qUnion([Q2]) }]});
        }
        {
            var Q0;
            Q0=qCreatedBy(makeId("Right.planeOp"),FACE);
            var sketch = newSketch(context, id + "F46", { "sketchPlane" : qUnion([Q0])});
            skPoint(sketch, "E108.start.orphan", {"position": v(0, 49.74) * mm});
            skPoint(sketch, "E109.start.orphan", {"position": v(0, 34.67) * mm});
            skLineSegment(sketch, "E110", {"start": v(25, 42.72) * mm, "end": v(25, 34.42) * mm});
            skLineSegment(sketch, "E111", {"start": v(25, 34.42) * mm, "end": v(0, 29.57) * mm});
            skLineSegment(sketch, "E112", {"start": v(0, 29.57) * mm, "end": v(-25, 34.42) * mm});
            skLineSegment(sketch, "E113", {"start": v(-25, 34.42) * mm, "end": v(-25, 42.72) * mm});
            skLineSegment(sketch, "E114", {"start": v(-25, 42.72) * mm, "end": v(0, 47.57) * mm});
            skLineSegment(sketch, "E115", {"start": v(0, 47.57) * mm, "end": v(25, 42.72) * mm});
            skLineSegment(sketch, "E116", {"start": v(0, 47.57) * mm, "end": v(0, 29.57) * mm, "construction": true});
            skLineSegment(sketch, "E117", {"start": v(-25, 38.57) * mm, "end": v(25, 38.57) * mm, "construction": true});
            skSolve(sketch);
        }
        {
            var Q0;
            Q0 = qSketchRegion(id + "F46", true);
            extrude(context, id + "F47", {"entities" : qUnion([Q0]), "operationType" : NewBodyOperationType.ADD, "depth" : 10 * mm});
        }
        {
            var Q0;
            Q0=makeQuery(id+"F47.opExtrude","CAP_FACE",FACE,{"disambiguationData":[OSD([sQuery(id+"F46.wireOp",EDGE,"E110"),sQuery(id+"F46.wireOp",EDGE,"E111"),sQuery(id+"F46.wireOp",EDGE,"E112"),sQuery(id+"F46.wireOp",EDGE,"E113"),sQuery(id+"F46.wireOp",EDGE,"E114"),sQuery(id+"F46.wireOp",EDGE,"E115")])],"isStart":false});
            extrude(context, id + "F48", {"entities" : qUnion([Q0]), "operationType" : NewBodyOperationType.ADD, "oppositeDirection" : true, "depth" : 20 * mm});
        }
        {
            var Q0;
            Q0 = qSketchRegion(id + "F16", true);
            var Q1;
            Q1 = qSketchRegion(id + "F18", true);
            var Q2;
            Q2 = qSketchRegion(id + "F23", true);
            var Q3;
            Q3 = qSketchRegion(id + "F25", true);
            extrude(context, id + "F49", {"entities" : qUnion([Q0, Q1, Q2, Q3]), "operationType" : NewBodyOperationType.REMOVE, "oppositeDirection" : true, "depth" : 1 * mm});
        }
        {
            var Q0;
            Q0 = qSketchRegion(id + "F15", true);
            extrude(context, id + "F50", {"entities" : qUnion([Q0]), "operationType" : NewBodyOperationType.REMOVE, "oppositeDirection" : true, "depth" : 1 * mm});
        }
    });
